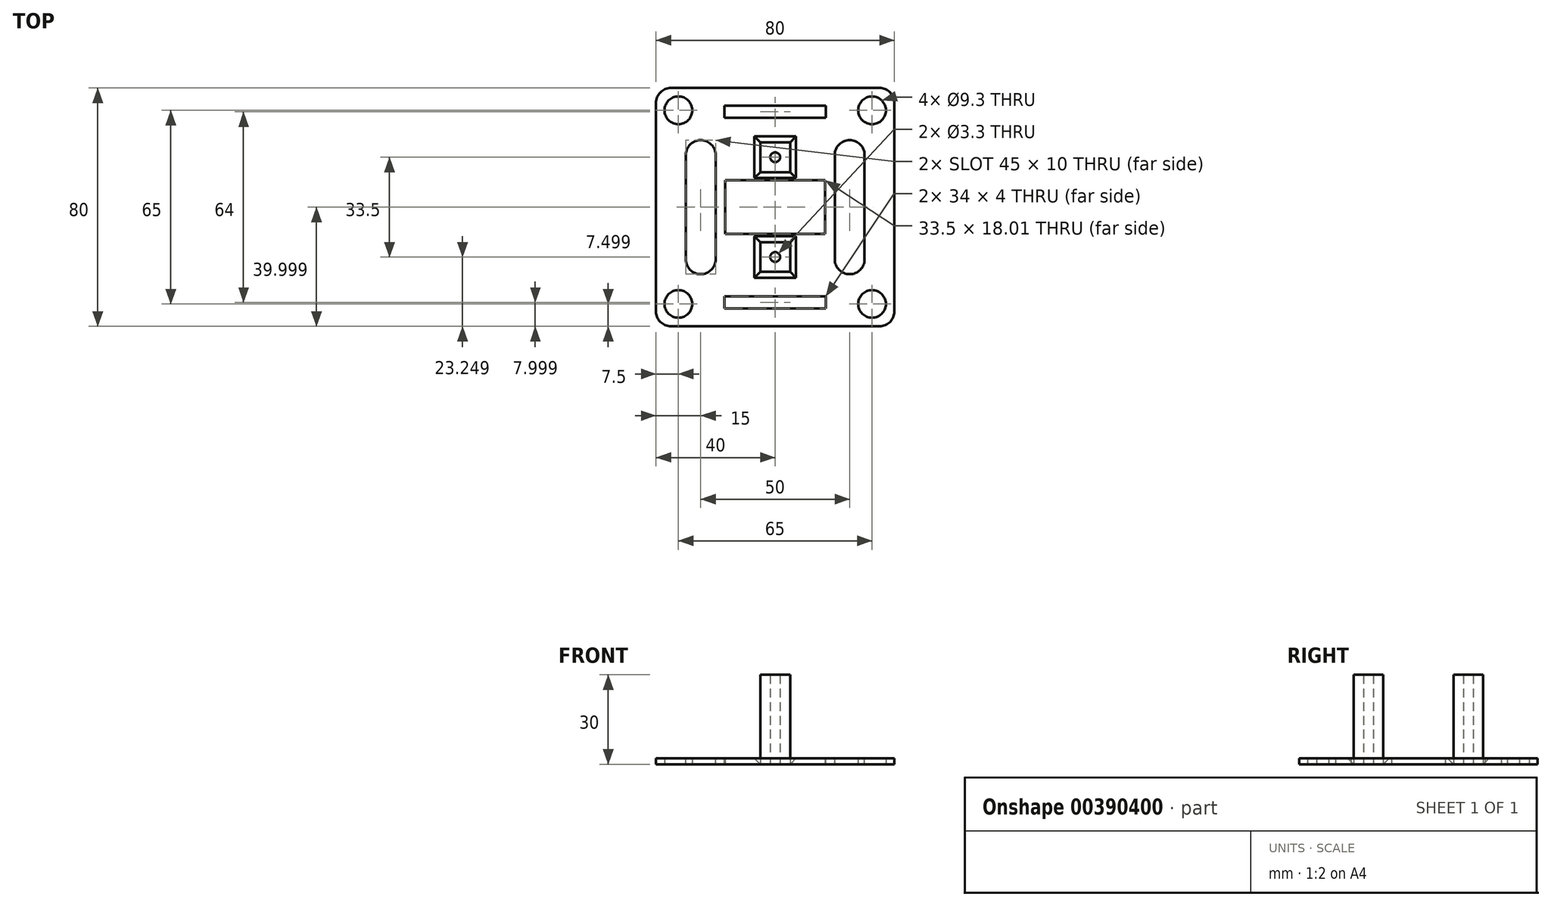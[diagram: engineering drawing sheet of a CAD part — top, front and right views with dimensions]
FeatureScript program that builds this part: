
annotation { "Feature Type Name" : "Feature", "Feature Type Description" : "" }
export const myFeature = defineFeature(function(context is Context, id is Id, definition is map)
    precondition{}
    {
        {
            var Q0;
            Q0=qCreatedBy(makeId("Top.planeOp"),FACE);
            var sketch = newSketch(context, id + "F0", { "sketchPlane" : qUnion([Q0])});
            skLineSegment(sketch, "E0.bottom", {"start": v(-40.42, -39.02) * mm, "end": v(39.58, -39.02) * mm});
            skLineSegment(sketch, "E0.top", {"start": v(-40.42, 40.98) * mm, "end": v(39.58, 40.98) * mm});
            skLineSegment(sketch, "E0.left", {"start": v(-40.42, -39.02) * mm, "end": v(-40.42, 40.98) * mm});
            skLineSegment(sketch, "E0.right", {"start": v(39.58, -39.02) * mm, "end": v(39.58, 40.98) * mm});
            skLineSegment(sketch, "E1", {"start": v(-0.42, 40.98) * mm, "end": v(-0.42, -39.02) * mm, "construction": true});
            skLineSegment(sketch, "E2", {"start": v(39.58, 0.98) * mm, "end": v(-40.42, 0.98) * mm, "construction": true});
            skLineSegment(sketch, "E3", {"start": v(7.08, 40.98) * mm, "end": v(7.08, -39.02) * mm, "construction": true});
            skLineSegment(sketch, "E4", {"start": v(-7.92, 40.98) * mm, "end": v(-7.92, -39.02) * mm, "construction": true});
            skLineSegment(sketch, "E5", {"start": v(39.58, 40.98) * mm, "end": v(-40.42, -39.02) * mm, "construction": true});
            skLineSegment(sketch, "E6", {"start": v(-40.42, 40.98) * mm, "end": v(39.58, -39.02) * mm, "construction": true});
            skLineSegment(sketch, "E7.bottom", {"start": v(-32.92, 33.48) * mm, "end": v(32.08, 33.48) * mm, "construction": true});
            skLineSegment(sketch, "E7.top", {"start": v(-32.92, -31.52) * mm, "end": v(32.08, -31.52) * mm, "construction": true});
            skLineSegment(sketch, "E7.left", {"start": v(-32.92, 33.48) * mm, "end": v(-32.92, -31.52) * mm, "construction": true});
            skLineSegment(sketch, "E7.right", {"start": v(32.08, 33.48) * mm, "end": v(32.08, -31.52) * mm, "construction": true});
            skLineSegment(sketch, "E8.bottom", {"start": v(-17.17, 17.73) * mm, "end": v(16.33, 17.73) * mm, "construction": true});
            skLineSegment(sketch, "E8.top", {"start": v(-17.17, -15.77) * mm, "end": v(16.33, -15.77) * mm, "construction": true});
            skLineSegment(sketch, "E8.left", {"start": v(-17.17, 17.73) * mm, "end": v(-17.17, -15.77) * mm, "construction": true});
            skLineSegment(sketch, "E8.right", {"start": v(16.33, 17.73) * mm, "end": v(16.33, -15.77) * mm, "construction": true});
            skLineSegment(sketch, "E9.bottom", {"start": v(-5.42, -10.77) * mm, "end": v(4.58, -10.77) * mm});
            skLineSegment(sketch, "E9.top", {"start": v(-5.42, -20.77) * mm, "end": v(4.58, -20.77) * mm});
            skLineSegment(sketch, "E9.left", {"start": v(-5.42, -10.77) * mm, "end": v(-5.42, -20.77) * mm});
            skLineSegment(sketch, "E9.right", {"start": v(4.58, -10.77) * mm, "end": v(4.58, -20.77) * mm});
            skLineSegment(sketch, "E10.bottom", {"start": v(-5.42, 22.73) * mm, "end": v(4.58, 22.73) * mm});
            skLineSegment(sketch, "E10.top", {"start": v(-5.42, 12.73) * mm, "end": v(4.58, 12.73) * mm});
            skLineSegment(sketch, "E10.left", {"start": v(-5.42, 22.73) * mm, "end": v(-5.42, 12.73) * mm});
            skLineSegment(sketch, "E10.right", {"start": v(4.58, 22.73) * mm, "end": v(4.58, 12.73) * mm});
            skLineSegment(sketch, "E11.bottom", {"start": v(16.33, 9.98) * mm, "end": v(-17.17, 9.98) * mm});
            skLineSegment(sketch, "E11.top", {"start": v(16.33, -8.03) * mm, "end": v(-17.17, -8.03) * mm});
            skLineSegment(sketch, "E11.left", {"start": v(16.33, 9.98) * mm, "end": v(16.33, -8.03) * mm});
            skLineSegment(sketch, "E11.right", {"start": v(-17.17, 9.98) * mm, "end": v(-17.17, -8.03) * mm});
            skCircle(sketch, "E12", {"center": v(-0.42, 17.73) * mm, "radius": 1.65 * mm});
            skCircle(sketch, "E13", {"center": v(-0.42, -15.77) * mm, "radius": 1.65 * mm});
            skCircle(sketch, "E14", {"center": v(32.08, 33.48) * mm, "radius": 4.65 * mm});
            skCircle(sketch, "E15", {"center": v(32.08, -31.52) * mm, "radius": 4.65 * mm});
            skCircle(sketch, "E16", {"center": v(-32.92, -31.52) * mm, "radius": 4.65 * mm});
            skCircle(sketch, "E17", {"center": v(-32.92, 33.48) * mm, "radius": 4.65 * mm});
            skSolve(sketch);
        }
        {
            var Q0;
            Q0=makeQuery(id+"F0.imprint","IMPRINT",FACE,{"disambiguationData":[TD([[makeQuery(id+"F0.imprint","IMPRINT",EDGE,{"derivedFrom":sQuery(id+"F0.wireOp",EDGE,"E10.bottom")}),-1.0]])]});
            var Q1;
            Q1=makeQuery(id+"F0.imprint","IMPRINT",FACE,{"disambiguationData":[TD([[makeQuery(id+"F0.imprint","IMPRINT",EDGE,{"derivedFrom":sQuery(id+"F0.wireOp",EDGE,"E9.bottom")}),-1.0]])]});
            extrude(context, id + "F1", {"entities" : qUnion([Q0, Q1]), "depth" : 30 * mm});
        }
        {
            var Q0;
            Q0=makeQuery(id+"F0.imprint","IMPRINT",FACE,{"disambiguationData":[TD([[makeQuery(id+"F0.imprint","IMPRINT",EDGE,{"derivedFrom":sQuery(id+"F0.wireOp",EDGE,"E0.bottom")}),1.0]])]});
            extrude(context, id + "F2", {"entities" : qUnion([Q0]), "depth" : 2 * mm});
        }
        {
            var Q0;
            Q0=makeQuery(id+"F2.opExtrude","SWEPT_EDGE",EDGE,{"disambiguationData":[OSD([sQuery(id+"F0.wireOp",EDGE,"E0.bottom"),sQuery(id+"F0.wireOp",EDGE,"E0.left")])]});
            var Q1;
            Q1=makeQuery(id+"F2.opExtrude","SWEPT_EDGE",EDGE,{"disambiguationData":[OSD([sQuery(id+"F0.wireOp",EDGE,"E0.top"),sQuery(id+"F0.wireOp",EDGE,"E0.left")])]});
            var Q2;
            Q2=makeQuery(id+"F2.opExtrude","SWEPT_EDGE",EDGE,{"disambiguationData":[OSD([sQuery(id+"F0.wireOp",EDGE,"E0.bottom"),sQuery(id+"F0.wireOp",EDGE,"E0.right")])]});
            var Q3;
            Q3=makeQuery(id+"F2.opExtrude","SWEPT_EDGE",EDGE,{"disambiguationData":[OSD([sQuery(id+"F0.wireOp",EDGE,"E0.top"),sQuery(id+"F0.wireOp",EDGE,"E0.right")])]});
            fillet(context, id + "F3", {"entities" : qUnion([Q0, Q1, Q2, Q3]), "radius" : 5 * mm, "tangentPropagation" : true, "allowEdgeOverflow" : false});
        }
        {
            var Q0;
            Q0=makeQuery(id+"F2.opExtrude","CAP_EDGE",EDGE,{"disambiguationData":[OSD([sQuery(id+"F0.wireOp",EDGE,"E10.bottom")])],"isStart":false});
            var Q1;
            Q1=makeQuery(id+"F2.opExtrude","CAP_EDGE",EDGE,{"disambiguationData":[OSD([sQuery(id+"F0.wireOp",EDGE,"E9.bottom")])],"isStart":false});
            var Q2;
            Q2=makeQuery(id+"F2.opExtrude","CAP_EDGE",EDGE,{"disambiguationData":[OSD([sQuery(id+"F0.wireOp",EDGE,"E9.right")])],"isStart":false});
            var Q3;
            Q3=makeQuery(id+"F2.opExtrude","CAP_EDGE",EDGE,{"disambiguationData":[OSD([sQuery(id+"F0.wireOp",EDGE,"E10.right")])],"isStart":false});
            var Q4;
            Q4=makeQuery(id+"F2.opExtrude","CAP_EDGE",EDGE,{"disambiguationData":[OSD([sQuery(id+"F0.wireOp",EDGE,"E9.top")])],"isStart":false});
            var Q5;
            Q5=makeQuery(id+"F2.opExtrude","CAP_EDGE",EDGE,{"disambiguationData":[OSD([sQuery(id+"F0.wireOp",EDGE,"E10.top")])],"isStart":false});
            var Q6;
            Q6=makeQuery(id+"F2.opExtrude","CAP_EDGE",EDGE,{"disambiguationData":[OSD([sQuery(id+"F0.wireOp",EDGE,"E10.left")])],"isStart":false});
            var Q7;
            Q7=makeQuery(id+"F2.opExtrude","CAP_EDGE",EDGE,{"disambiguationData":[OSD([sQuery(id+"F0.wireOp",EDGE,"E9.left")])],"isStart":false});
            chamfer(context, id + "F4", {"entities" : qUnion([Q0, Q1, Q2, Q3, Q4, Q5, Q6, Q7]), "width" : 2 * mm, "tangentPropagation" : true});
        }
        {
            var Q0;
            Q0=makeQuery(id+"F2.opExtrude","CAP_FACE",FACE,{"disambiguationData":[OSD([sQuery(id+"F0.wireOp",EDGE,"E0.bottom"),sQuery(id+"F0.wireOp",EDGE,"E0.top"),sQuery(id+"F0.wireOp",EDGE,"E0.left"),sQuery(id+"F0.wireOp",EDGE,"E0.right"),sQuery(id+"F0.wireOp",EDGE,"E9.bottom"),sQuery(id+"F0.wireOp",EDGE,"E9.top"),sQuery(id+"F0.wireOp",EDGE,"E9.left"),sQuery(id+"F0.wireOp",EDGE,"E9.right"),sQuery(id+"F0.wireOp",EDGE,"E10.bottom"),sQuery(id+"F0.wireOp",EDGE,"E10.top"),sQuery(id+"F0.wireOp",EDGE,"E10.left"),sQuery(id+"F0.wireOp",EDGE,"E10.right"),sQuery(id+"F0.wireOp",EDGE,"E11.bottom"),sQuery(id+"F0.wireOp",EDGE,"E11.top"),sQuery(id+"F0.wireOp",EDGE,"E11.left"),sQuery(id+"F0.wireOp",EDGE,"E11.right"),sQuery(id+"F0.wireOp",EDGE,"E14"),sQuery(id+"F0.wireOp",EDGE,"E15"),sQuery(id+"F0.wireOp",EDGE,"E16"),sQuery(id+"F0.wireOp",EDGE,"E17")])],"isStart":false});
            var sketch = newSketch(context, id + "F5", { "sketchPlane" : qUnion([Q0])});
            skLineSegment(sketch, "E18", {"start": v(16.33, 0.98) * mm, "end": v(39.58, 0.98) * mm, "construction": true});
            skLineSegment(sketch, "E19", {"start": v(-17.17, 0.98) * mm, "end": v(-40.42, 0.98) * mm, "construction": true});
            skLineSegment(sketch, "E20", {"start": v(-0.42, 24.73) * mm, "end": v(-0.42, 40.98) * mm, "construction": true});
            skLineSegment(sketch, "E21", {"start": v(-0.42, -22.77) * mm, "end": v(-0.42, -39.02) * mm, "construction": true});
            skLineSegment(sketch, "E22.bottom", {"start": v(24.58, 23.48) * mm, "end": v(24.58, 23.48) * mm});
            skLineSegment(sketch, "E22.top", {"start": v(24.58, -21.52) * mm, "end": v(24.58, -21.52) * mm});
            skLineSegment(sketch, "E22.left", {"start": v(19.58, 18.48) * mm, "end": v(19.58, -16.52) * mm});
            skLineSegment(sketch, "E22.right", {"start": v(29.58, 18.48) * mm, "end": v(29.58, -16.52) * mm});
            skLineSegment(sketch, "E23.bottom", {"start": v(-25.42, 23.48) * mm, "end": v(-25.42, 23.48) * mm});
            skLineSegment(sketch, "E23.top", {"start": v(-25.42, -21.52) * mm, "end": v(-25.42, -21.52) * mm});
            skLineSegment(sketch, "E23.left", {"start": v(-20.42, 18.48) * mm, "end": v(-20.42, -16.52) * mm});
            skLineSegment(sketch, "E23.right", {"start": v(-30.42, 18.48) * mm, "end": v(-30.42, -16.52) * mm});
            skPoint(sketch, "E24.visualSharp", {"position": v(-30.42, 23.48) * mm});
            skArc(sketch, "E24.filletArc", {"start": v(-25.42, 23.48) * mm, "mid": v(-28.96, 22.01) * mm, "end": v(-30.42, 18.48) * mm});
            skPoint(sketch, "E25.visualSharp", {"position": v(-20.42, 23.48) * mm});
            skArc(sketch, "E25.filletArc", {"start": v(-20.42, 18.48) * mm, "mid": v(-21.88, 22.01) * mm, "end": v(-25.42, 23.48) * mm});
            skPoint(sketch, "E26.visualSharp", {"position": v(-30.42, -21.52) * mm});
            skArc(sketch, "E26.filletArc", {"start": v(-30.42, -16.52) * mm, "mid": v(-28.96, -20.06) * mm, "end": v(-25.42, -21.52) * mm});
            skPoint(sketch, "E27.visualSharp", {"position": v(-20.42, -21.52) * mm});
            skArc(sketch, "E27.filletArc", {"start": v(-25.42, -21.52) * mm, "mid": v(-21.88, -20.06) * mm, "end": v(-20.42, -16.52) * mm});
            skPoint(sketch, "E28.visualSharp", {"position": v(19.58, 23.48) * mm});
            skArc(sketch, "E28.filletArc", {"start": v(24.58, 23.48) * mm, "mid": v(21.04, 22.01) * mm, "end": v(19.58, 18.48) * mm});
            skPoint(sketch, "E29.visualSharp", {"position": v(29.58, 23.48) * mm});
            skArc(sketch, "E29.filletArc", {"start": v(29.58, 18.48) * mm, "mid": v(28.12, 22.01) * mm, "end": v(24.58, 23.48) * mm});
            skPoint(sketch, "E30.visualSharp", {"position": v(29.58, -21.52) * mm});
            skArc(sketch, "E30.filletArc", {"start": v(24.58, -21.52) * mm, "mid": v(28.12, -20.06) * mm, "end": v(29.58, -16.52) * mm});
            skPoint(sketch, "E31.visualSharp", {"position": v(19.58, -21.52) * mm});
            skArc(sketch, "E31.filletArc", {"start": v(19.58, -16.52) * mm, "mid": v(21.04, -20.06) * mm, "end": v(24.58, -21.52) * mm});
            skLineSegment(sketch, "E32.bottom", {"start": v(-17.42, 34.98) * mm, "end": v(16.58, 34.98) * mm});
            skLineSegment(sketch, "E32.top", {"start": v(-17.42, 30.98) * mm, "end": v(16.58, 30.98) * mm});
            skLineSegment(sketch, "E32.left", {"start": v(-17.42, 34.98) * mm, "end": v(-17.42, 30.98) * mm});
            skLineSegment(sketch, "E32.right", {"start": v(16.58, 34.98) * mm, "end": v(16.58, 30.98) * mm});
            skLineSegment(sketch, "E33.bottom", {"start": v(-17.42, -29.02) * mm, "end": v(16.58, -29.02) * mm});
            skLineSegment(sketch, "E33.top", {"start": v(-17.42, -33.02) * mm, "end": v(16.58, -33.02) * mm});
            skLineSegment(sketch, "E33.left", {"start": v(-17.42, -29.02) * mm, "end": v(-17.42, -33.02) * mm});
            skLineSegment(sketch, "E33.right", {"start": v(16.58, -29.02) * mm, "end": v(16.58, -33.02) * mm});
            skSolve(sketch);
        }
        {
            var Q0;
            Q0=makeQuery(id+"F5.imprint","IMPRINT",FACE,{"disambiguationData":[TD([[makeQuery(id+"F5.imprint","IMPRINT",EDGE,{"derivedFrom":sQuery(id+"F5.wireOp",EDGE,"E23.left")}),-1.0]])]});
            var Q1;
            Q1=makeQuery(id+"F5.imprint","IMPRINT",FACE,{"disambiguationData":[TD([[makeQuery(id+"F5.imprint","IMPRINT",EDGE,{"derivedFrom":sQuery(id+"F5.wireOp",EDGE,"E32.bottom")}),-1.0]])]});
            var Q2;
            Q2=makeQuery(id+"F5.imprint","IMPRINT",FACE,{"disambiguationData":[TD([[makeQuery(id+"F5.imprint","IMPRINT",EDGE,{"derivedFrom":sQuery(id+"F5.wireOp",EDGE,"E22.left")}),1.0]])]});
            var Q3;
            Q3=makeQuery(id+"F5.imprint","IMPRINT",FACE,{"disambiguationData":[TD([[makeQuery(id+"F5.imprint","IMPRINT",EDGE,{"derivedFrom":sQuery(id+"F5.wireOp",EDGE,"E33.bottom")}),-1.0]])]});
            extrude(context, id + "F6", {"entities" : qUnion([Q0, Q1, Q2, Q3]), "operationType" : NewBodyOperationType.REMOVE, "oppositeDirection" : true, "depth" : 25 * mm});
        }
    });
